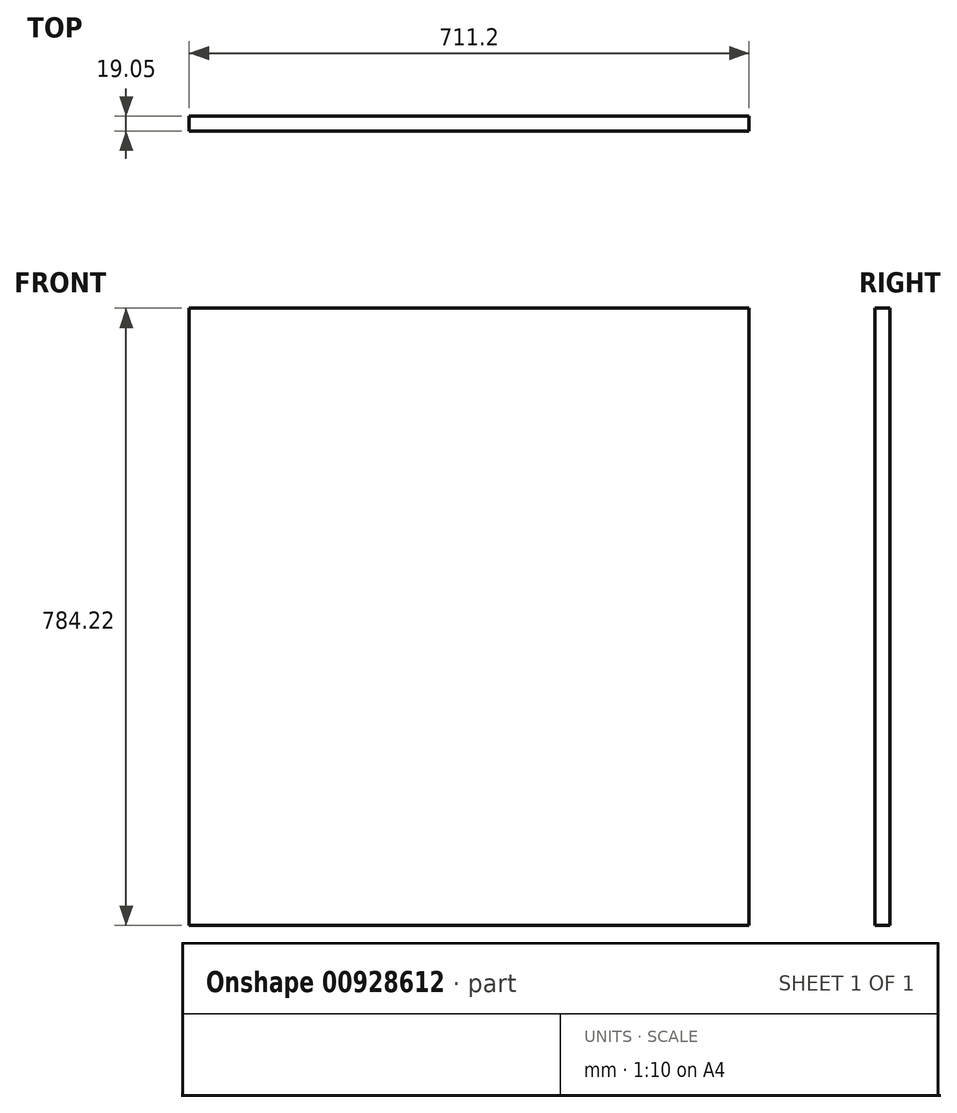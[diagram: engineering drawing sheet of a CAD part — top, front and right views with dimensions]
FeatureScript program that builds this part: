
annotation { "Feature Type Name" : "Feature", "Feature Type Description" : "" }
export const myFeature = defineFeature(function(context is Context, id is Id, definition is map)
    precondition{}
    {
        {
            var Q0;
            Q0=qCreatedBy(makeId("Front.planeOp"),FACE);
            var sketch = newSketch(context, id + "F0", { "sketchPlane" : qUnion([Q0])});
            skLineSegment(sketch, "E0.bottom", {"start": v(355.6, 392.11) * mm, "end": v(-355.6, 392.11) * mm});
            skLineSegment(sketch, "E0.top", {"start": v(355.6, -392.11) * mm, "end": v(-355.6, -392.11) * mm});
            skLineSegment(sketch, "E0.left", {"start": v(355.6, 392.11) * mm, "end": v(355.6, -392.11) * mm});
            skLineSegment(sketch, "E0.right", {"start": v(-355.6, 392.11) * mm, "end": v(-355.6, -392.11) * mm});
            skPoint(sketch, "E0.middle", {"position": v(0, 0) * mm});
            skSolve(sketch);
        }
        {
            var Q0;
            Q0=makeQuery(id+"F0.imprint","IMPRINT",FACE,{"disambiguationData":[TD([[makeQuery(id+"F0.imprint","IMPRINT",EDGE,{"derivedFrom":sQuery(id+"F0.wireOp",EDGE,"E0.bottom")}),1.0]])]});
            extrude(context, id + "F1", {"entities" : qUnion([Q0]), "depth" : 19.05 * mm, "offsetDistance" : 25.4 * mm});
        }
    });
